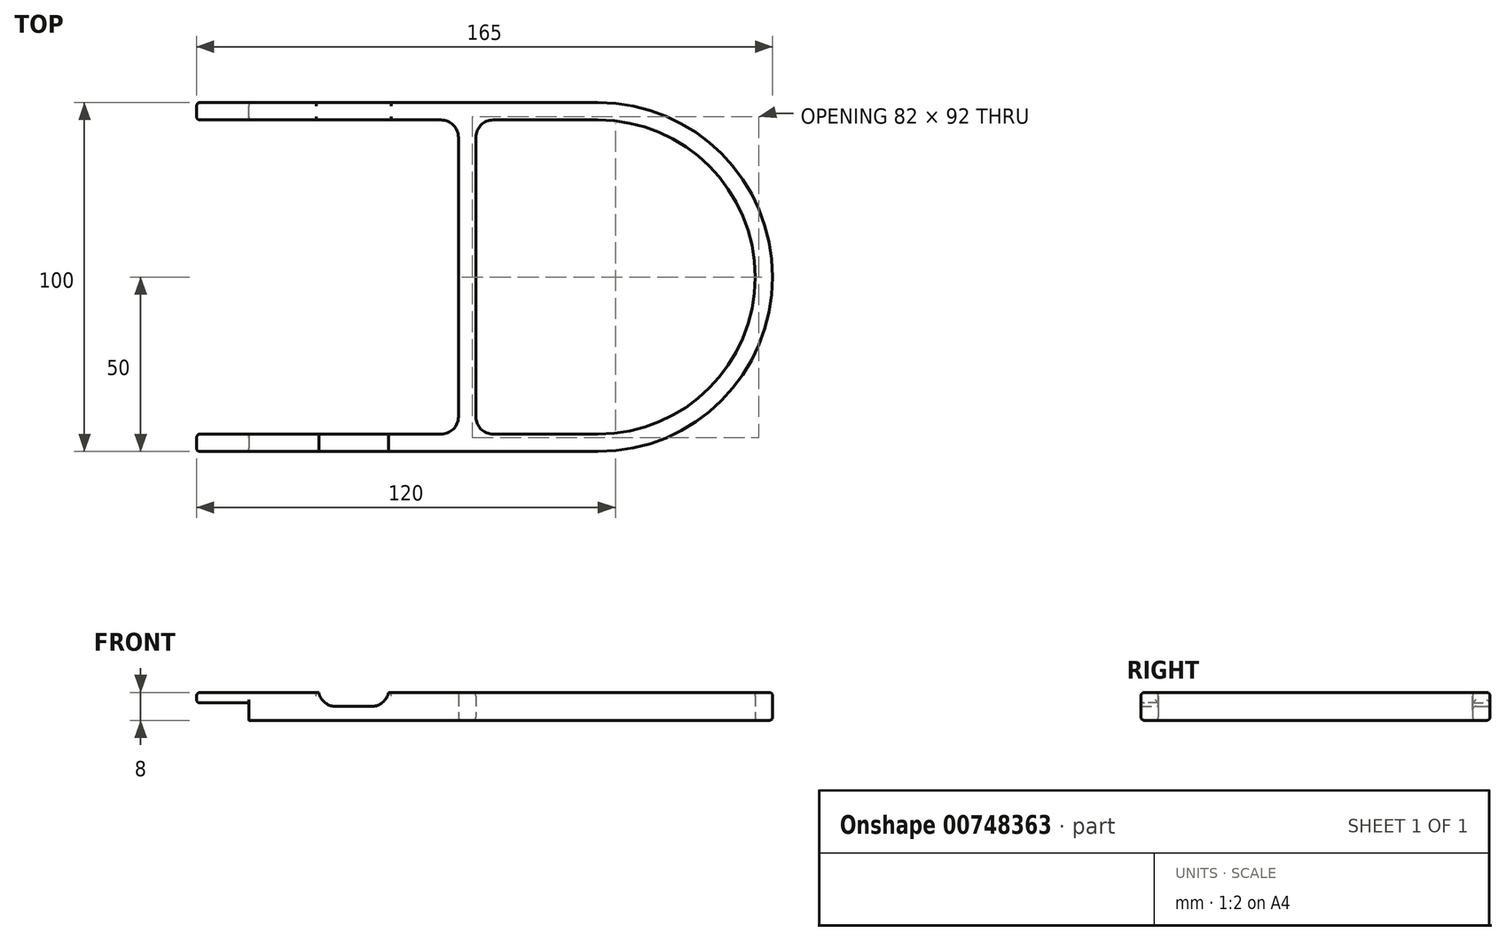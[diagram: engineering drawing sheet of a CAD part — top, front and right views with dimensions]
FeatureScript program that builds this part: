
annotation { "Feature Type Name" : "Feature", "Feature Type Description" : "" }
export const myFeature = defineFeature(function(context is Context, id is Id, definition is map)
    precondition{}
    {
        {
            var Q0;
            Q0=qCreatedBy(makeId("Top.planeOp"),FACE);
            var sketch = newSketch(context, id + "F0", { "sketchPlane" : qUnion([Q0])});
            skLineSegment(sketch, "E0", {"start": v(0, 0) * mm, "end": v(100, 0) * mm});
            skArc(sketch, "E1", {"start": v(100, 0) * mm, "mid": v(145, 45) * mm, "end": v(100, 90) * mm});
            skLineSegment(sketch, "E2", {"start": v(100, 90) * mm, "end": v(0, 90) * mm});
            skLineSegment(sketch, "E3", {"start": v(0, 90) * mm, "end": v(0, 95) * mm});
            skLineSegment(sketch, "E4", {"start": v(0, 95) * mm, "end": v(100, 95) * mm});
            skArc(sketch, "E5", {"start": v(100, -5) * mm, "mid": v(150, 45) * mm, "end": v(100, 95) * mm});
            skLineSegment(sketch, "E6", {"start": v(0, 0) * mm, "end": v(0, -5) * mm});
            skLineSegment(sketch, "E7", {"start": v(0, -5) * mm, "end": v(100, -5) * mm});
            skLineSegment(sketch, "E8.bottom", {"start": v(60, 0) * mm, "end": v(65, 0) * mm});
            skLineSegment(sketch, "E8.top", {"start": v(60, 90) * mm, "end": v(65, 90) * mm});
            skLineSegment(sketch, "E8.left", {"start": v(60, 0) * mm, "end": v(60, 90) * mm});
            skLineSegment(sketch, "E8.right", {"start": v(65, 0) * mm, "end": v(65, 90) * mm});
            skSolve(sketch);
        }
        {
            var Q0;
            Q0=qSketchRegion(id+"F0",true);
            extrude(context, id + "F1", {"entities" : qUnion([Q0]), "depth" : 8 * mm, "offsetDistance" : 25 * mm});
        }
        {
            var Q0;
            Q0=makeQuery(id+"F1.opExtrude","SWEPT_FACE",FACE,{"disambiguationData":[OSD([sQuery(id+"F0.wireOp",EDGE,"E6")])]});
            var sketch = newSketch(context, id + "F2", { "sketchPlane" : qUnion([Q0])});
            skLineSegment(sketch, "E9.bottom", {"start": v(0, 8) * mm, "end": v(5, 8) * mm});
            skLineSegment(sketch, "E9.top", {"start": v(0, 5) * mm, "end": v(5, 5) * mm});
            skLineSegment(sketch, "E9.left", {"start": v(0, 8) * mm, "end": v(0, 5) * mm});
            skLineSegment(sketch, "E9.right", {"start": v(5, 8) * mm, "end": v(5, 5) * mm});
            skLineSegment(sketch, "E10.bottom", {"start": v(-90, 5) * mm, "end": v(-95, 5) * mm});
            skLineSegment(sketch, "E10.top", {"start": v(-90, 8) * mm, "end": v(-95, 8) * mm});
            skLineSegment(sketch, "E10.left", {"start": v(-90, 5) * mm, "end": v(-90, 8) * mm});
            skLineSegment(sketch, "E10.right", {"start": v(-95, 5) * mm, "end": v(-95, 8) * mm});
            skSolve(sketch);
        }
        {
            var Q0;
            Q0=qSketchRegion(id+"F2",true);
            extrude(context, id + "F3", {"entities" : qUnion([Q0]), "operationType" : NewBodyOperationType.ADD, "depth" : 15 * mm, "offsetDistance" : 25 * mm});
        }
        {
            var Q0;
            Q0=makeQuery(id+"F1.opExtrude","SWEPT_EDGE",EDGE,{"disambiguationData":[OSD([sQuery(id+"F0.wireOp",EDGE,"E2"),sQuery(id+"F0.wireOp",EDGE,"E8.top"),sQuery(id+"F0.wireOp",EDGE,"E8.left")])]});
            var Q1;
            Q1=makeQuery(id+"F1.opExtrude","SWEPT_EDGE",EDGE,{"disambiguationData":[OSD([sQuery(id+"F0.wireOp",EDGE,"E2"),sQuery(id+"F0.wireOp",EDGE,"E8.top"),sQuery(id+"F0.wireOp",EDGE,"E8.right")])]});
            var Q2;
            Q2=makeQuery(id+"F1.opExtrude","SWEPT_EDGE",EDGE,{"disambiguationData":[OSD([sQuery(id+"F0.wireOp",EDGE,"E0"),sQuery(id+"F0.wireOp",EDGE,"E8.bottom"),sQuery(id+"F0.wireOp",EDGE,"E8.right")])]});
            var Q3;
            Q3=makeQuery(id+"F1.opExtrude","SWEPT_EDGE",EDGE,{"disambiguationData":[OSD([sQuery(id+"F0.wireOp",EDGE,"E0"),sQuery(id+"F0.wireOp",EDGE,"E8.bottom"),sQuery(id+"F0.wireOp",EDGE,"E8.left")])]});
            fillet(context, id + "F4", {"entities" : qUnion([Q0, Q1, Q2, Q3]), "radius" : 5 * mm, "tangentPropagation" : true, "allowEdgeOverflow" : false});
        }
        {
            var Q0;
            Q0=makeQuery(id+"F3.boolean.opBoolean","MERGE",FACE,{"derivedFrom":[makeQuery(id+"F1.opExtrude","SWEPT_FACE",FACE,{"disambiguationData":[OSD([sQuery(id+"F0.wireOp",EDGE,"E7")])]}),makeQuery(id+"F3.opExtrude","SWEPT_FACE",FACE,{"disambiguationData":[OSD([sQuery(id+"F2.wireOp",EDGE,"E9.right")])]})]});
            var sketch = newSketch(context, id + "F5", { "sketchPlane" : qUnion([Q0])});
            skLineSegment(sketch, "E11.bottom", {"start": v(20, 8) * mm, "end": v(40, 8) * mm});
            skLineSegment(sketch, "E11.top", {"start": v(20, 4) * mm, "end": v(40, 4) * mm});
            skLineSegment(sketch, "E11.left", {"start": v(20, 8) * mm, "end": v(20, 4) * mm});
            skLineSegment(sketch, "E11.right", {"start": v(40, 8) * mm, "end": v(40, 4) * mm});
            skSolve(sketch);
        }
        {
            var Q0;
            Q0=qSketchRegion(id+"F5",true);
            extrude(context, id + "F6", {"entities" : qUnion([Q0]), "operationType" : NewBodyOperationType.REMOVE, "endBound" : BoundingType.THROUGH_ALL, "oppositeDirection" : true, "depth" : 25 * mm, "offsetDistance" : 25 * mm});
        }
        {
            var Q0;
            {var subQ1=sQuery(id+"F5.wireOp",EDGE,"E11.top");var subQ2=sQuery(id+"F5.wireOp",EDGE,"E11.left");Q0=makeQuery(id+"F6.boolean.opBoolean","COPY",EDGE,{"disambiguationData":[TD([makeQuery(id+"F1.opExtrude","SWEPT_FACE",FACE,{"disambiguationData":[OSD([sQuery(id+"F0.wireOp",EDGE,"E4")])]})])],"derivedFrom":makeQuery(id+"F6.opExtrude","SWEPT_EDGE",EDGE,{"disambiguationData":[OSD([subQ1,subQ2])]})});}
            var Q1;
            {var subQ1=sQuery(id+"F5.wireOp",EDGE,"E11.top");var subQ2=sQuery(id+"F5.wireOp",EDGE,"E11.right");Q1=makeQuery(id+"F6.boolean.opBoolean","COPY",EDGE,{"disambiguationData":[TD([makeQuery(id+"F1.opExtrude","SWEPT_FACE",FACE,{"disambiguationData":[OSD([sQuery(id+"F0.wireOp",EDGE,"E4")])]})])],"derivedFrom":makeQuery(id+"F6.opExtrude","SWEPT_EDGE",EDGE,{"disambiguationData":[OSD([subQ1,subQ2])]})});}
            var Q2;
            {var subQ1=sQuery(id+"F5.wireOp",EDGE,"E11.top");var subQ2=sQuery(id+"F5.wireOp",EDGE,"E11.right");Q2=makeQuery(id+"F6.boolean.opBoolean","COPY",EDGE,{"disambiguationData":[TD([makeQuery(id+"F1.opExtrude","SWEPT_FACE",FACE,{"disambiguationData":[OSD([sQuery(id+"F0.wireOp",EDGE,"E7")])]})])],"derivedFrom":makeQuery(id+"F6.opExtrude","SWEPT_EDGE",EDGE,{"disambiguationData":[OSD([subQ1,subQ2])]})});}
            var Q3;
            {var subQ1=sQuery(id+"F5.wireOp",EDGE,"E11.top");var subQ2=sQuery(id+"F5.wireOp",EDGE,"E11.left");Q3=makeQuery(id+"F6.boolean.opBoolean","COPY",EDGE,{"disambiguationData":[TD([makeQuery(id+"F1.opExtrude","SWEPT_FACE",FACE,{"disambiguationData":[OSD([sQuery(id+"F0.wireOp",EDGE,"E7")])]})])],"derivedFrom":makeQuery(id+"F6.opExtrude","SWEPT_EDGE",EDGE,{"disambiguationData":[OSD([subQ1,subQ2])]})});}
            var Q4;
            Q4=makeQuery(id+"F3.opExtrude","CAP_EDGE",EDGE,{"disambiguationData":[OSD([sQuery(id+"F2.wireOp",EDGE,"E9.top")])],"isStart":true});
            var Q5;
            Q5=makeQuery(id+"F3.opExtrude","CAP_EDGE",EDGE,{"disambiguationData":[OSD([sQuery(id+"F2.wireOp",EDGE,"E10.bottom")])],"isStart":true});
            fillet(context, id + "F7", {"entities" : qUnion([Q0, Q1, Q2, Q3, Q4, Q5]), "radius" : 5 * mm, "tangentPropagation" : true, "allowEdgeOverflow" : false});
        }
        {
            var Q0;
            {var subQ0=sQuery(id+"F0.wireOp",EDGE,"E2");Q0=makeQuery(id+"F1.opExtrude","CAP_EDGE",EDGE,{"disambiguationData":[OSD([subQ0]),TDD([makeQuery(id+"F0.imprint","IMPRINT",EDGE,{"disambiguationData":[TD([[makeQuery(id+"F0.imprint","INTERSECT",VERTEX,{"derivedFrom":[sQuery(id+"F0.wireOp",EDGE,"E1"),subQ0]}),-1.0]])],"derivedFrom":subQ0})])],"isStart":false});}
            var Q1;
            {var subQ0=sQuery(id+"F0.wireOp",EDGE,"E3");var subQ1=sQuery(id+"F0.wireOp",EDGE,"E2");var subQ4=makeQuery(id+"F0.imprint","IMPRINT",EDGE,{"disambiguationData":[TD([[makeQuery(id+"F0.imprint","INTERSECT",VERTEX,{"derivedFrom":[subQ1,subQ0]}),1.0]])],"derivedFrom":subQ1});var subQ5=sQuery(id+"F2.wireOp",EDGE,"E10.top");var subQ6=sQuery(id+"F2.wireOp",EDGE,"E10.left");Q1=makeQuery(id+"F6.boolean.opBoolean","SPLIT",EDGE,{"disambiguationData":[TD([makeQuery(id+"F6.opExtrude","SWEPT_FACE",FACE,{"disambiguationData":[OSD([sQuery(id+"F5.wireOp",EDGE,"E11.right")])]})])],"derivedFrom":makeQuery(id+"F3.boolean.opBoolean","MERGE",EDGE,{"derivedFrom":[makeQuery(id+"F1.opExtrude","CAP_EDGE",EDGE,{"disambiguationData":[OSD([subQ1]),TDD([subQ4])],"isStart":false}),makeQuery(id+"F3.opExtrude","SWEPT_EDGE",EDGE,{"disambiguationData":[OSD([subQ5,subQ6])]})]})});}
            var Q2;
            {var subQ0=sQuery(id+"F2.wireOp",EDGE,"E9.bottom");var subQ1=sQuery(id+"F0.wireOp",EDGE,"E7");var subQ2=sQuery(id+"F0.wireOp",EDGE,"E5");var subQ3=sQuery(id+"F2.wireOp",EDGE,"E9.right");Q2=makeQuery(id+"F6.boolean.opBoolean","SPLIT",EDGE,{"disambiguationData":[TD([makeQuery(id+"F1.opExtrude","SWEPT_FACE",FACE,{"disambiguationData":[OSD([subQ2])]})])],"derivedFrom":makeQuery(id+"F3.boolean.opBoolean","MERGE",EDGE,{"derivedFrom":[makeQuery(id+"F1.opExtrude","CAP_EDGE",EDGE,{"disambiguationData":[OSD([subQ1])],"isStart":false}),makeQuery(id+"F3.opExtrude","SWEPT_EDGE",EDGE,{"disambiguationData":[OSD([subQ0,subQ3])]})]})});}
            var Q3;
            Q3=makeQuery(id+"F1.opExtrude","CAP_EDGE",EDGE,{"disambiguationData":[OSD([sQuery(id+"F0.wireOp",EDGE,"E7")])],"isStart":true});
            var Q4;
            {var subQ0=sQuery(id+"F0.wireOp",EDGE,"E0");Q4=makeQuery(id+"F1.opExtrude","CAP_EDGE",EDGE,{"disambiguationData":[OSD([subQ0]),TDD([makeQuery(id+"F0.imprint","IMPRINT",EDGE,{"disambiguationData":[TD([[makeQuery(id+"F0.imprint","INTERSECT",VERTEX,{"derivedFrom":[subQ0,sQuery(id+"F0.wireOp",EDGE,"E1")]}),1.0]])],"derivedFrom":subQ0})])],"isStart":true});}
            var Q5;
            {var subQ0=sQuery(id+"F0.wireOp",EDGE,"E0");Q5=makeQuery(id+"F1.opExtrude","CAP_EDGE",EDGE,{"disambiguationData":[OSD([subQ0]),TDD([makeQuery(id+"F0.imprint","IMPRINT",EDGE,{"disambiguationData":[TD([[makeQuery(id+"F0.imprint","INTERSECT",VERTEX,{"derivedFrom":[subQ0,sQuery(id+"F0.wireOp",EDGE,"E6")]}),-1.0]])],"derivedFrom":subQ0})])],"isStart":true});}
            var Q6;
            {var subQ0=sQuery(id+"F2.wireOp",EDGE,"E9.bottom");var subQ2=sQuery(id+"F0.wireOp",EDGE,"E6");var subQ3=sQuery(id+"F0.wireOp",EDGE,"E0");var subQ4=sQuery(id+"F2.wireOp",EDGE,"E9.left");var subQ5=makeQuery(id+"F0.imprint","IMPRINT",EDGE,{"disambiguationData":[TD([[makeQuery(id+"F0.imprint","INTERSECT",VERTEX,{"derivedFrom":[subQ3,subQ2]}),-1.0]])],"derivedFrom":subQ3});Q6=makeQuery(id+"F6.boolean.opBoolean","SPLIT",EDGE,{"disambiguationData":[TD([makeQuery(id+"F6.opExtrude","SWEPT_FACE",FACE,{"disambiguationData":[OSD([sQuery(id+"F5.wireOp",EDGE,"E11.left")])]})])],"derivedFrom":makeQuery(id+"F3.boolean.opBoolean","MERGE",EDGE,{"derivedFrom":[makeQuery(id+"F1.opExtrude","CAP_EDGE",EDGE,{"disambiguationData":[OSD([subQ3]),TDD([subQ5])],"isStart":false}),makeQuery(id+"F3.opExtrude","SWEPT_EDGE",EDGE,{"disambiguationData":[OSD([subQ0,subQ4])]})]})});}
            var Q7;
            {var subQ0=sQuery(id+"F2.wireOp",EDGE,"E9.right");var subQ1=sQuery(id+"F2.wireOp",EDGE,"E9.bottom");var subQ2=sQuery(id+"F0.wireOp",EDGE,"E7");Q7=makeQuery(id+"F6.boolean.opBoolean","SPLIT",EDGE,{"disambiguationData":[TD([makeQuery(id+"F6.opExtrude","SWEPT_FACE",FACE,{"disambiguationData":[OSD([sQuery(id+"F5.wireOp",EDGE,"E11.left")])]})])],"derivedFrom":makeQuery(id+"F3.boolean.opBoolean","MERGE",EDGE,{"derivedFrom":[makeQuery(id+"F1.opExtrude","CAP_EDGE",EDGE,{"disambiguationData":[OSD([subQ2])],"isStart":false}),makeQuery(id+"F3.opExtrude","SWEPT_EDGE",EDGE,{"disambiguationData":[OSD([subQ1,subQ0])]})]})});}
            var Q8;
            {var subQ0=sQuery(id+"F2.wireOp",EDGE,"E10.right");var subQ1=sQuery(id+"F2.wireOp",EDGE,"E10.top");var subQ2=sQuery(id+"F0.wireOp",EDGE,"E4");Q8=makeQuery(id+"F6.boolean.opBoolean","SPLIT",EDGE,{"disambiguationData":[TD([makeQuery(id+"F6.opExtrude","SWEPT_FACE",FACE,{"disambiguationData":[OSD([sQuery(id+"F5.wireOp",EDGE,"E11.left")])]})])],"derivedFrom":makeQuery(id+"F3.boolean.opBoolean","MERGE",EDGE,{"derivedFrom":[makeQuery(id+"F1.opExtrude","CAP_EDGE",EDGE,{"disambiguationData":[OSD([subQ2])],"isStart":false}),makeQuery(id+"F3.opExtrude","SWEPT_EDGE",EDGE,{"disambiguationData":[OSD([subQ1,subQ0])]})]})});}
            var Q9;
            {var subQ0=sQuery(id+"F2.wireOp",EDGE,"E10.left");var subQ1=sQuery(id+"F2.wireOp",EDGE,"E10.top");var subQ2=sQuery(id+"F0.wireOp",EDGE,"E3");var subQ3=sQuery(id+"F0.wireOp",EDGE,"E2");var subQ5=makeQuery(id+"F0.imprint","IMPRINT",EDGE,{"disambiguationData":[TD([[makeQuery(id+"F0.imprint","INTERSECT",VERTEX,{"derivedFrom":[subQ3,subQ2]}),1.0]])],"derivedFrom":subQ3});Q9=makeQuery(id+"F6.boolean.opBoolean","SPLIT",EDGE,{"disambiguationData":[TD([makeQuery(id+"F6.opExtrude","SWEPT_FACE",FACE,{"disambiguationData":[OSD([sQuery(id+"F5.wireOp",EDGE,"E11.left")])]})])],"derivedFrom":makeQuery(id+"F3.boolean.opBoolean","MERGE",EDGE,{"derivedFrom":[makeQuery(id+"F1.opExtrude","CAP_EDGE",EDGE,{"disambiguationData":[OSD([subQ3]),TDD([subQ5])],"isStart":false}),makeQuery(id+"F3.opExtrude","SWEPT_EDGE",EDGE,{"disambiguationData":[OSD([subQ1,subQ0])]})]})});}
            fillet(context, id + "F8", {"entities" : qUnion([Q0, Q1, Q2, Q3, Q4, Q5, Q6, Q7, Q8, Q9]), "radius" : 1 * mm, "tangentPropagation" : true, "allowEdgeOverflow" : false});
        }
        {
            var Q0;
            {var subQ0=sQuery(id+"F0.wireOp",EDGE,"E2");Q0=makeQuery(id+"F6.boolean.opBoolean","INTERSECT",EDGE,{"derivedFrom":[makeQuery(id+"F3.boolean.opBoolean","MERGE",FACE,{"derivedFrom":[makeQuery(id+"F1.opExtrude","SWEPT_FACE",FACE,{"disambiguationData":[OSD([subQ0]),TDD([makeQuery(id+"F0.imprint","IMPRINT",EDGE,{"disambiguationData":[TD([[makeQuery(id+"F0.imprint","INTERSECT",VERTEX,{"derivedFrom":[subQ0,sQuery(id+"F0.wireOp",EDGE,"E3")]}),1.0]])],"derivedFrom":subQ0})])]}),makeQuery(id+"F3.opExtrude","SWEPT_FACE",FACE,{"disambiguationData":[OSD([sQuery(id+"F2.wireOp",EDGE,"E10.left")])]})]}),makeQuery(id+"F6.opExtrude","SWEPT_FACE",FACE,{"disambiguationData":[OSD([sQuery(id+"F5.wireOp",EDGE,"E11.top")])]})]});}
            var Q1;
            Q1=makeQuery(id+"F6.boolean.opBoolean","COPY",EDGE,{"derivedFrom":makeQuery(id+"F6.opExtrude","CAP_EDGE",EDGE,{"disambiguationData":[OSD([sQuery(id+"F5.wireOp",EDGE,"E11.top")])],"isStart":true})});
            var Q2;
            Q2=makeQuery(id+"F3.opExtrude","SWEPT_EDGE",EDGE,{"disambiguationData":[OSD([sQuery(id+"F0.wireOp",EDGE,"E6"),sQuery(id+"F0.wireOp",EDGE,"E7"),sQuery(id+"F2.wireOp",EDGE,"E9.top"),sQuery(id+"F2.wireOp",EDGE,"E9.right")])]});
            var Q3;
            {var subQ0=sQuery(id+"F0.wireOp",EDGE,"E2");Q3=makeQuery(id+"F7.opFillet","BLEND_EDGE",EDGE,{"blendedFrom":[makeQuery(id+"F3.opExtrude","CAP_EDGE",EDGE,{"disambiguationData":[OSD([sQuery(id+"F2.wireOp",EDGE,"E10.bottom")])],"isStart":true}),makeQuery(id+"F3.boolean.opBoolean","MERGE",FACE,{"derivedFrom":[makeQuery(id+"F1.opExtrude","SWEPT_FACE",FACE,{"disambiguationData":[OSD([subQ0]),TDD([makeQuery(id+"F0.imprint","IMPRINT",EDGE,{"disambiguationData":[TD([[makeQuery(id+"F0.imprint","INTERSECT",VERTEX,{"derivedFrom":[subQ0,sQuery(id+"F0.wireOp",EDGE,"E3")]}),1.0]])],"derivedFrom":subQ0})])]}),makeQuery(id+"F3.opExtrude","SWEPT_FACE",FACE,{"disambiguationData":[OSD([sQuery(id+"F2.wireOp",EDGE,"E10.left")])]})]})],"blendedInto":[makeQuery(id+"F3.boolean.opBoolean","MERGE",FACE,{"derivedFrom":[makeQuery(id+"F1.opExtrude","SWEPT_FACE",FACE,{"disambiguationData":[OSD([subQ0]),TDD([makeQuery(id+"F0.imprint","IMPRINT",EDGE,{"disambiguationData":[TD([[makeQuery(id+"F0.imprint","INTERSECT",VERTEX,{"derivedFrom":[subQ0,sQuery(id+"F0.wireOp",EDGE,"E3")]}),1.0]])],"derivedFrom":subQ0})])]}),makeQuery(id+"F3.opExtrude","SWEPT_FACE",FACE,{"disambiguationData":[OSD([sQuery(id+"F2.wireOp",EDGE,"E10.left")])]})]})]});}
            var Q4;
            Q4=makeQuery(id+"F3.opExtrude","CAP_FACE",FACE,{"disambiguationData":[OSD([sQuery(id+"F2.wireOp",EDGE,"E9.bottom"),sQuery(id+"F2.wireOp",EDGE,"E9.top"),sQuery(id+"F2.wireOp",EDGE,"E9.left"),sQuery(id+"F2.wireOp",EDGE,"E9.right")])],"isStart":false});
            var Q5;
            Q5=makeQuery(id+"F3.opExtrude","CAP_FACE",FACE,{"disambiguationData":[OSD([sQuery(id+"F2.wireOp",EDGE,"E10.bottom"),sQuery(id+"F2.wireOp",EDGE,"E10.top"),sQuery(id+"F2.wireOp",EDGE,"E10.left"),sQuery(id+"F2.wireOp",EDGE,"E10.right")])],"isStart":false});
            fillet(context, id + "F9", {"entities" : qUnion([Q0, Q1, Q2, Q3, Q4, Q5]), "radius" : 1 * mm, "tangentPropagation" : true, "allowEdgeOverflow" : false});
        }
    });
